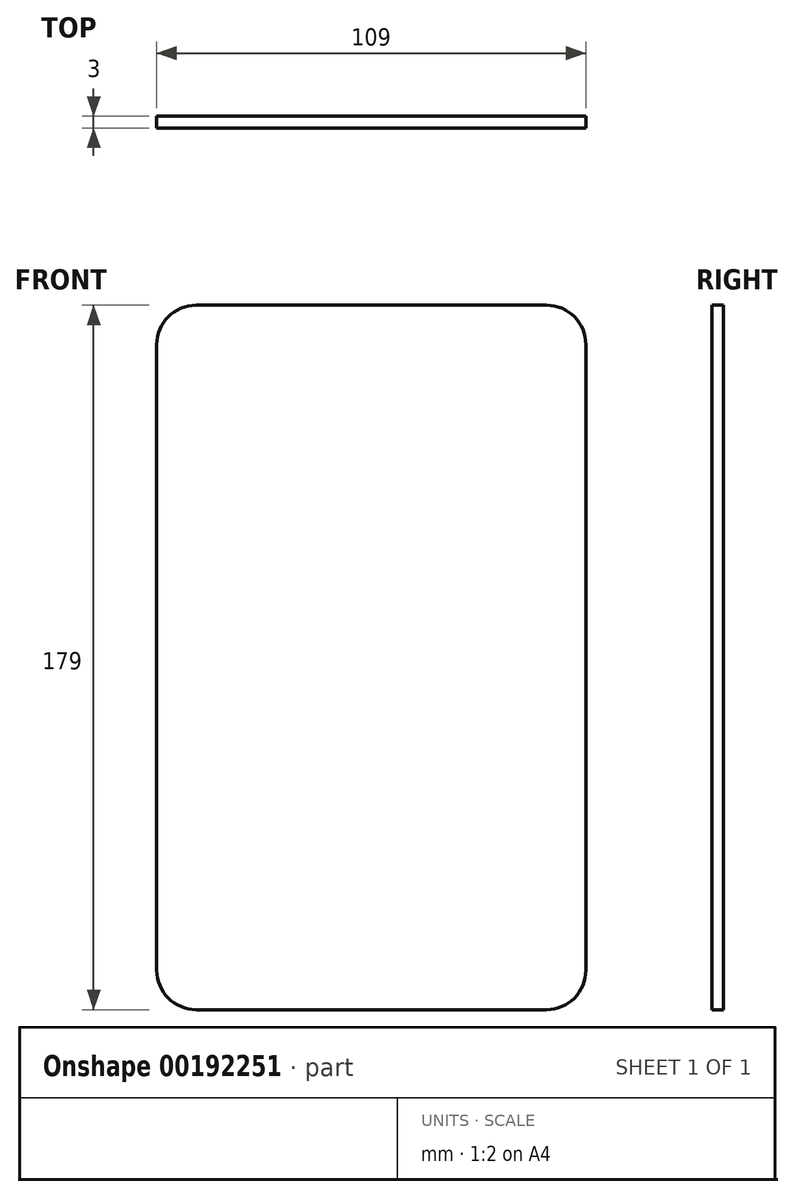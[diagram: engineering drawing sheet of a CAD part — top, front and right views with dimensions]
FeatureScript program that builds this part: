
annotation { "Feature Type Name" : "Feature", "Feature Type Description" : "" }
export const myFeature = defineFeature(function(context is Context, id is Id, definition is map)
    precondition{}
    {
        {
            var Q0;
            Q0=qCreatedBy(makeId("Front.planeOp"),FACE);
            var sketch = newSketch(context, id + "F0", { "sketchPlane" : qUnion([Q0])});
            skLineSegment(sketch, "E0.bottom", {"start": v(54.5, -89.5) * mm, "end": v(-54.5, -89.5) * mm});
            skLineSegment(sketch, "E0.top", {"start": v(54.5, 89.5) * mm, "end": v(-54.5, 89.5) * mm});
            skLineSegment(sketch, "E0.left", {"start": v(54.5, -89.5) * mm, "end": v(54.5, 89.5) * mm});
            skLineSegment(sketch, "E0.right", {"start": v(-54.5, -89.5) * mm, "end": v(-54.5, 89.5) * mm});
            skPoint(sketch, "E0.middle", {"position": v(0, 0) * mm});
            skSolve(sketch);
        }
        {
            var Q0;
            Q0=makeQuery(id+"F0.imprint","IMPRINT",FACE,{"disambiguationData":[TD([[makeQuery(id+"F0.imprint","IMPRINT",EDGE,{"derivedFrom":sQuery(id+"F0.wireOp",EDGE,"E0.bottom")}),-1.0]])]});
            extrude(context, id + "F1", {"entities" : qUnion([Q0]), "depth" : 3 * mm});
        }
        {
            var Q0;
            Q0=makeQuery(id+"F1.opExtrude","SWEPT_EDGE",EDGE,{"disambiguationData":[OSD([sQuery(id+"F0.wireOp",EDGE,"E0.top"),sQuery(id+"F0.wireOp",EDGE,"E0.left")])]});
            var Q1;
            Q1=makeQuery(id+"F1.opExtrude","SWEPT_EDGE",EDGE,{"disambiguationData":[OSD([sQuery(id+"F0.wireOp",EDGE,"E0.top"),sQuery(id+"F0.wireOp",EDGE,"E0.right")])]});
            var Q2;
            Q2=makeQuery(id+"F1.opExtrude","SWEPT_EDGE",EDGE,{"disambiguationData":[OSD([sQuery(id+"F0.wireOp",EDGE,"E0.bottom"),sQuery(id+"F0.wireOp",EDGE,"E0.left")])]});
            var Q3;
            Q3=makeQuery(id+"F1.opExtrude","SWEPT_EDGE",EDGE,{"disambiguationData":[OSD([sQuery(id+"F0.wireOp",EDGE,"E0.bottom"),sQuery(id+"F0.wireOp",EDGE,"E0.right")])]});
            fillet(context, id + "F2", {"entities" : qUnion([Q0, Q1, Q2, Q3]), "radius" : 10 * mm, "tangentPropagation" : true, "allowEdgeOverflow" : false});
        }
    });
